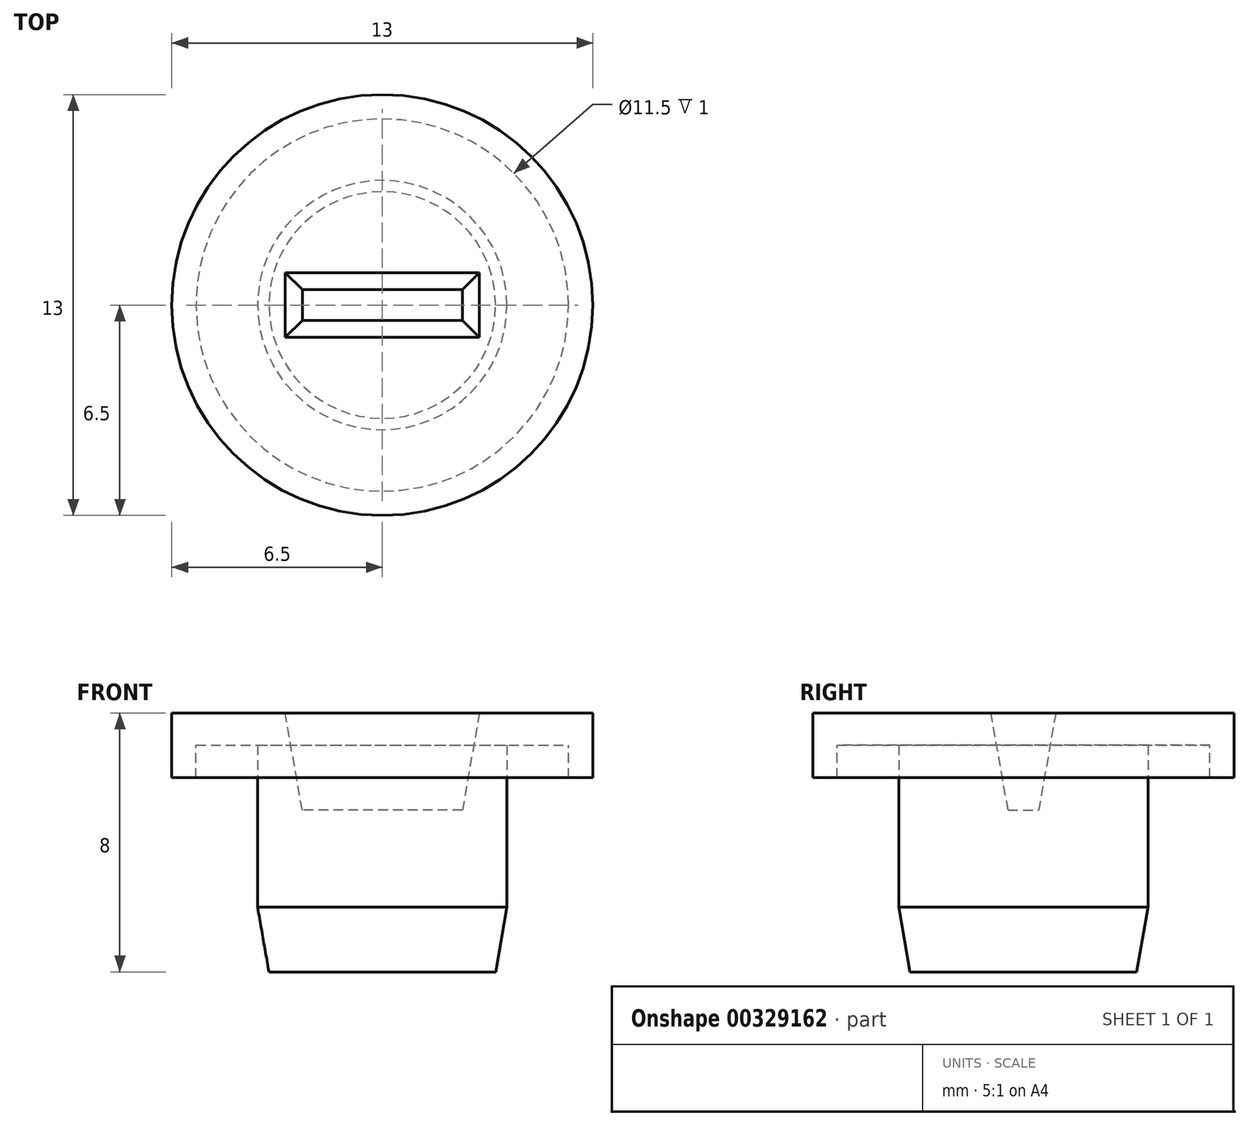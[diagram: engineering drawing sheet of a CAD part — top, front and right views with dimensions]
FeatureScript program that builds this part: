
annotation { "Feature Type Name" : "Feature", "Feature Type Description" : "" }
export const myFeature = defineFeature(function(context is Context, id is Id, definition is map)
    precondition{}
    {
        {
            var Q0;
            Q0=qCreatedBy(makeId("Right.planeOp"),FACE);
            var sketch = newSketch(context, id + "F0", { "sketchPlane" : qUnion([Q0])});
            skLineSegment(sketch, "E0", {"start": v(0, -17.82) * mm, "end": v(0, 30.83) * mm, "construction": true});
            skLineSegment(sketch, "E1", {"start": v(0, 0) * mm, "end": v(3.5, 0) * mm});
            skLineSegment(sketch, "E2", {"start": v(3.85, 0) * mm, "end": v(3.85, 7) * mm, "construction": true});
            skLineSegment(sketch, "E3", {"start": v(3.85, 7) * mm, "end": v(6.5, 7) * mm});
            skLineSegment(sketch, "E4", {"start": v(6.5, 7) * mm, "end": v(6.5, 8) * mm});
            skLineSegment(sketch, "E5", {"start": v(6.5, 8) * mm, "end": v(0, 8) * mm});
            skLineSegment(sketch, "E6", {"start": v(0, 8) * mm, "end": v(0, 0) * mm});
            skLineSegment(sketch, "E7", {"start": v(3.5, 0) * mm, "end": v(3.85, 0) * mm, "construction": true});
            skLineSegment(sketch, "E8", {"start": v(3.5, 0) * mm, "end": v(3.85, 2) * mm});
            skLineSegment(sketch, "E9", {"start": v(3.85, 2) * mm, "end": v(3.85, 7) * mm});
            skSolve(sketch);
        }
        {
            var Q0;
            Q0 = qSketchRegion(id + "F0", true);
            var Q1;
            Q1=sQuery(id+"F0.wireOp",EDGE,"E0");
            revolve(context, id + "F1", {"entities" : qUnion([Q0]), "axis" : qUnion([Q1]), "revolveType" : RevolveType.FULL});
        }
        {
            var Q0;
            Q0=makeQuery(id+"F1.opRevolve","SWEPT_FACE",FACE,{"disambiguationData":[OSD([sQuery(id+"F0.wireOp",EDGE,"E3")])]});
            var sketch = newSketch(context, id + "F2", { "sketchPlane" : qUnion([Q0])});
            skCircle(sketch, "E10.0", {"center": v(0, 0) * mm, "radius": 6.5 * mm});
            skCircle(sketch, "E11", {"center": v(0, 0) * mm, "radius": 5.75 * mm});
            skSolve(sketch);
        }
        {
            var Q0;
            Q0 = qSketchRegion(id + "F2", true);
            extrude(context, id + "F3", {"entities" : qUnion([Q0]), "operationType" : NewBodyOperationType.ADD, "depth" : 1 * mm});
        }
        {
            var Q0;
            Q0=makeQuery(id+"F1.opRevolve","SWEPT_FACE",FACE,{"disambiguationData":[OSD([sQuery(id+"F0.wireOp",EDGE,"E5")])]});
            var sketch = newSketch(context, id + "F4", { "sketchPlane" : qUnion([Q0])});
            skLineSegment(sketch, "E12.bottom", {"start": v(3, 1) * mm, "end": v(-3, 1) * mm});
            skLineSegment(sketch, "E12.top", {"start": v(3, -1) * mm, "end": v(-3, -1) * mm});
            skLineSegment(sketch, "E12.left", {"start": v(3, 1) * mm, "end": v(3, -1) * mm});
            skLineSegment(sketch, "E12.right", {"start": v(-3, 1) * mm, "end": v(-3, -1) * mm});
            skPoint(sketch, "E12.middle", {"position": v(0, 0) * mm});
            skSolve(sketch);
        }
        {
            var Q0;
            Q0 = qSketchRegion(id + "F4", true);
            extrude(context, id + "F5", {"entities" : qUnion([Q0]), "operationType" : NewBodyOperationType.REMOVE, "oppositeDirection" : true, "depth" : 3 * mm, "hasDraft" : true, "draftAngle" : 10 * degree, "draftPullDirection" : true});
        }
    });
